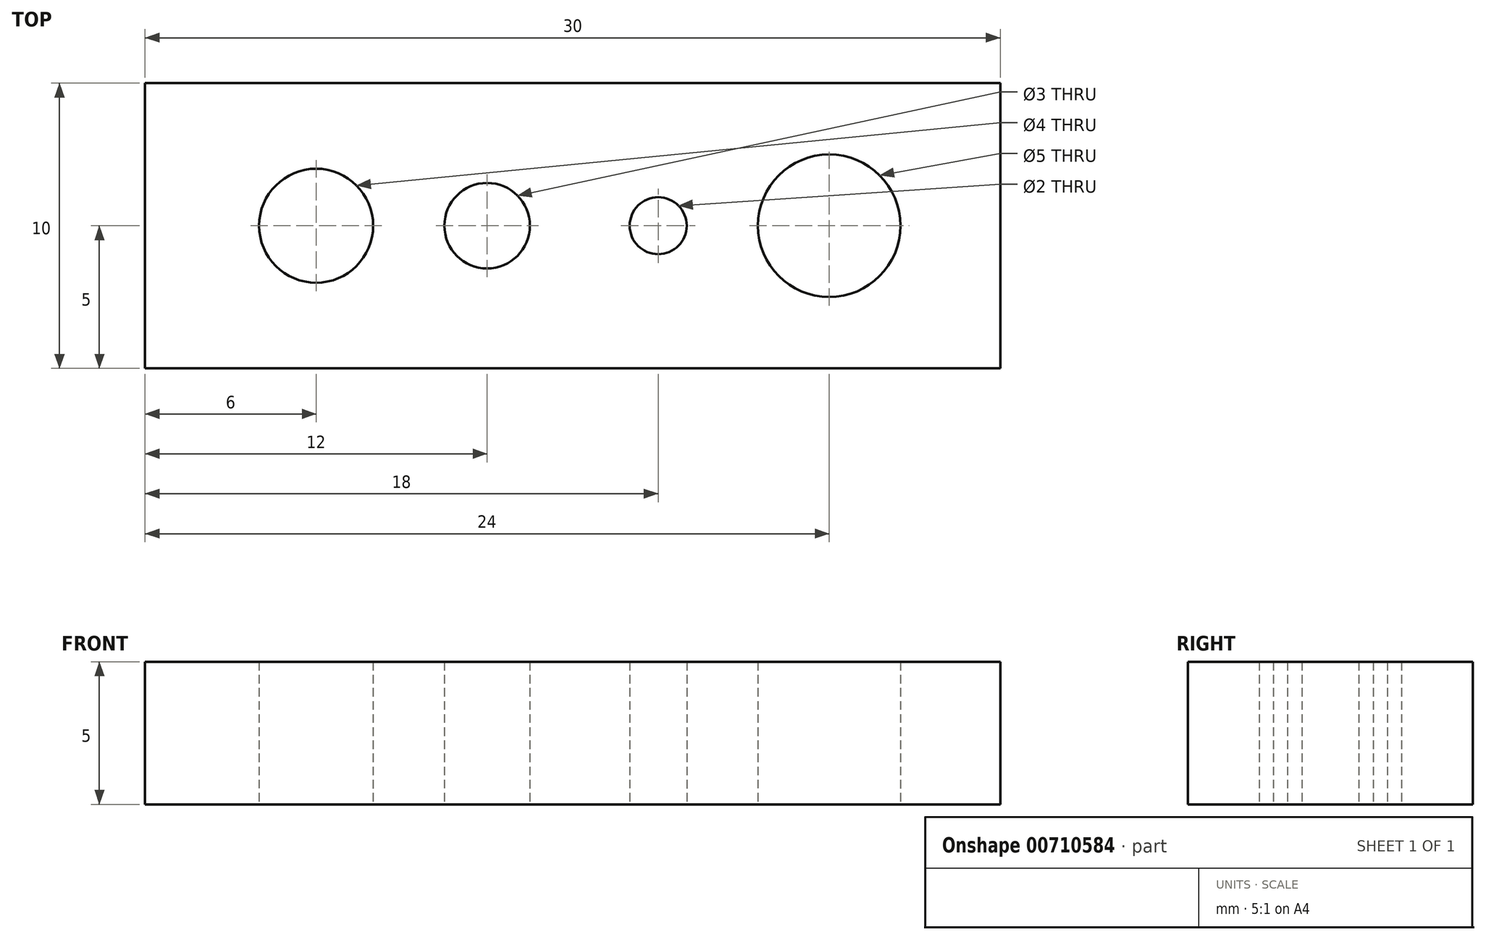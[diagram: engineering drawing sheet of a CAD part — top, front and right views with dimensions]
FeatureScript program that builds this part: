
annotation { "Feature Type Name" : "Feature", "Feature Type Description" : "" }
export const myFeature = defineFeature(function(context is Context, id is Id, definition is map)
    precondition{}
    {
        {
            var Q0;
            Q0=qCreatedBy(makeId("Top.planeOp"),FACE);
            var sketch = newSketch(context, id + "F0", { "sketchPlane" : qUnion([Q0])});
            skLineSegment(sketch, "E0.bottom", {"start": v(15, -5) * mm, "end": v(-15, -5) * mm});
            skLineSegment(sketch, "E0.top", {"start": v(15, 5) * mm, "end": v(-15, 5) * mm});
            skLineSegment(sketch, "E0.left", {"start": v(15, -5) * mm, "end": v(15, 5) * mm});
            skLineSegment(sketch, "E0.right", {"start": v(-15, -5) * mm, "end": v(-15, 5) * mm});
            skPoint(sketch, "E0.middle", {"position": v(0, 0) * mm});
            skLineSegment(sketch, "E1", {"start": v(-15, 0) * mm, "end": v(15, 0) * mm, "construction": true});
            skLineSegment(sketch, "E2", {"start": v(-15, 0) * mm, "end": v(-9, 0) * mm});
            skLineSegment(sketch, "E3", {"start": v(-9, 0) * mm, "end": v(-3, 0) * mm, "construction": true});
            skLineSegment(sketch, "E4", {"start": v(-3, 0) * mm, "end": v(3, 0) * mm, "construction": true});
            skLineSegment(sketch, "E5", {"start": v(3, 0) * mm, "end": v(9, 0) * mm});
            skCircle(sketch, "E6", {"center": v(-9, 0) * mm, "radius": 2 * mm});
            skCircle(sketch, "E7", {"center": v(-3, 0) * mm, "radius": 1.5 * mm});
            skCircle(sketch, "E8", {"center": v(3, 0) * mm, "radius": 1 * mm});
            skCircle(sketch, "E9", {"center": v(9, 0) * mm, "radius": 2.5 * mm});
            skSolve(sketch);
        }
        {
            var Q0;
            {var subQ1=sQuery(id+"F0.wireOp",EDGE,"E0.bottom");Q0=makeQuery(id+"F0.imprint","IMPRINT",FACE,{"disambiguationData":[TD([[makeQuery(id+"F0.imprint","IMPRINT",EDGE,{"derivedFrom":subQ1}),-1.0]])]});}
            extrude(context, id + "F1", {"entities" : qUnion([Q0]), "depth" : 5 * mm, "offsetDistance" : 25 * mm});
        }
    });
